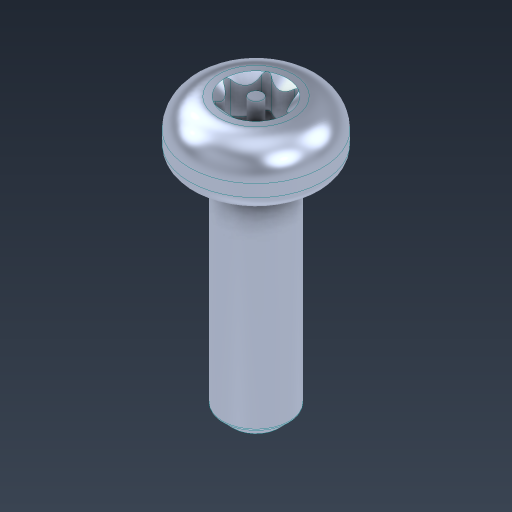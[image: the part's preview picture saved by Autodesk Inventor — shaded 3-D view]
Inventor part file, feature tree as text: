
AUTODESK INVENTOR PART (.ipt)
format: ipt  version: 2024.3 (Build 283343000, 343)  size: 198,144 bytes
history: native  units: in
note: dims shown in document units (in); Inventor stores cm internally (conversion verified against a paired STEP export)
features: fillet x1
ambient origin geometry x8: Origin, YZ Plane, XZ Plane, XY Plane, X Axis, Y Axis, Z Axis, Center Point
bodies: Solid1 (feature_tree)
feature tree (1):
  fillet  "Fillet3"  [1 undecoded]
note: 1 required parameter value undecoded (feature->parameter linkage not recoverable at this tier; creation-order binding heuristic only, values carry confidence <= 0.55)
